# Revit family: Legrand_Gestion_eclairage_Detecteur_Presence_Plafond_SCS
name_source: partatom
category: Dispositifs d'éclairage
units: mm (PartAtom-declared; Revit-internal decimal feet)

## family parameters
Conserver l'orientation des annotations = Non
Cote de connecteur circulaire = Utiliser le diamètre
Couper avec des vides une fois chargée = Non
Hôte = Face
Partagée = Non
Point de calcul de pièce = Non
Type d'élément = Normal

## types (2) — shared parameters
Adapté pour transmission sans fil = Non
Angle de détection horizontal (MAX) (°) = 360
Collecteur de terre = Non
Condition Générale d'Utilisation = https://export.legrand.com
Cosses d'artère secondaire = Non
Couleur = Blanc
Coupure forcée = Non
Durée d'enclenchement max. (mn) = 256
Durée d'enclenchement min. (s) = 30
Elévation par défaut = 1219 mm
Entrée secondaire = Non
Exécution - Modèle = détecteur de mouvement
Fabricant = Legrand
Fonction variateur intégré = Non
Gestion CVC = Non
Gestion alarme = Non
Hauteur de montage maximale (m) = 2.5
Liaison neutre = Non
Mode de montage = encastré
Numéro RAL = 9003
Portée max. latérale (m) = 4
Réglage de lumière constante = Oui
Sensibilité lumineuse réglable = Oui
Sensibilité réglable = Oui
Télécommandable = Non
URL = http://www.legrandoc.com
zero-valued in all types: Angle de détection horizontal (MIN) (°), Capacité de coupure max. (W), Courant de démarrage max. (A), Fréquence (MAX) (Hz), Fréquence (MIN) (Hz), Portée max. frontale (m), Sensibilité lumineuse (MAX) (lx), Sensibilité lumineuse (MIN) (lx), Température (MAX) (°C), Température (MIN) (°C), Tension nominale (V)

## per-type parameters (varying)
| type | Description | Diamètre de détection sur le plancher (m) | Modèle | Mouvement SCS PIR 360° 4m | Présence SCS PIR/US 360° 4m |
| Mouvement SCS PIR 360° 4m | Détect ECO BUS/SCS gestion éclair Prog Mosaic - faux plafond - IR - 45m² | 8 | 048820 | Oui | Non |
| Présence SCS PIR/US 360° 4m | Détect ECO BUS/SCS gestion éclair Prog Mosaic - faux plafond - IR/US-90 m² | 11 | 048822 | Non | Oui |
